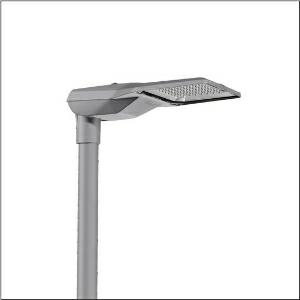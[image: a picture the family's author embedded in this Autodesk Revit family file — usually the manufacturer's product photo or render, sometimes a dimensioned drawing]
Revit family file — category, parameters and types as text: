
# Revit family: streetlight_sl_21_midi___st0_5a_5xe3b43s08lb_de93
name_source: partatom
category: Lighting Fixtures
units: mm (PartAtom-declared; Revit-internal decimal feet)

## family parameters
Cut with Voids When Loaded = No
Host = Face
Light Source = No
Part Type = Normal
Room Calculation Point = No
Round Connector Dimension = Use Diameter
Shared = No

## types (1)
- --- (1 x LED, 14950 lm, 99.6 W, 4000K)
    Apparent Load = 100 VA
    CIE Flux Codes = 41 75 97 100 100
    Color Rendering = 70
    Color Temperature = 4000K
    Default Elevation = 1800 mm
    Description = Streetlight SL 21 midi, mast luminaire, primary light control with lens, of PMMA, primary optical cover: cover, of toughened safety glass, transparent, light distribution: ST0.5a, light emission: direct distribution, primary light characteristic: asymmetric, installation type: side-entry, post-top, LED, High Power LED, rated luminous flux: 14.950lm, luminous efficacy: 150lm/W, light colour: 740, colour temperature: 4000K, control gear: D4i, control: overheat protection, constant luminous flux control, time-dependent luminous flux control, flexible luminous flux parameterisation, pre-setting: logarithmic dimming characteristic, mains connection: 230..240V, AC, 50/60Hz, start of lifetime: 100W, end of service life: 102W, reduction: 46W, luminaire housing, of diecast aluminium, powder-coated, SITECO metallic grey (DB 702S), corrosivity category C5 high according to DIN EN ISO 12944, please order mast flange separately, inclination adjustable: 0°, 5°, 10°, 15°, sealing non-destructively replaceable, multi-level sealing system, length: 644mm, width: 335mm, height: 110mm, mast flange for spigot size: 42mm (side-entry): 5XC10008XM4, 60/48mm (side-entry/post-top): 5XC10108XM2, 76/60mm (side-entry/post-top): 5XC10108XM1, mounting height: 4..8m, Smart Interface above, protection rating (complete): IP66, insulation class (complete): insulation class II (safety insulation), certification: CE, ENEC, ENEC+, VDE, impact resistance: IK10, permissible operating ambient temperature for outdoor applications: -40..+50°C, standard-compliant lighting for roads and squares, packaging unit: 1 piece

Light Distribution: ST0.5a
    Height = 111 mm
    Lamp = 1 x LED
    Lamp Light Flux = 14950 lm
    Lamp Power = 99.6 W
    Lamp count = 1
    Length = 644 mm
    Luminous efficacy = 150 lm/W
    Manufacturer = Siteco
    ModVariant = No
    Model = 5XE3B43S08LB
    Number of Poles = 1
    OnlyDefault = Yes
    Power Factor = 1
    Product Name = Streetlight SL 21 midi | ST0.5a
    Product group = mast luminaire | pylon top
    ProductGroupID = 6100
    Protection Class = Protection class II
    Protection Degree = IP 66
    RLX_Detail_Level = 1
    RLX_Emergency_Light_Flux = 0 lm
    RLX_Emergency_Type = 0
    RLX_Emergency_Type_DB = No
    RlxData = <blob elided: 37865 chars, md5=10960e66>
    Socket = socket
    Standby Power = 0 W
    System Light Flux = 14950 lm
    System Power = 100 W
    Type Comments = factory setting: luminous flux: 100 % | dim-lin: 254 | 1020 mA
    Type Image = l_1004302.jpg
    URL = http://relux.com
    VarID = @adj_032337
    Voltage = 0 V
    Weight = 0.00 kg
    Width = 336 mm

## geometry (parser evidence)
native form markers: Blend x4, Sweep x9
no freeform markers — native parametric forms only
